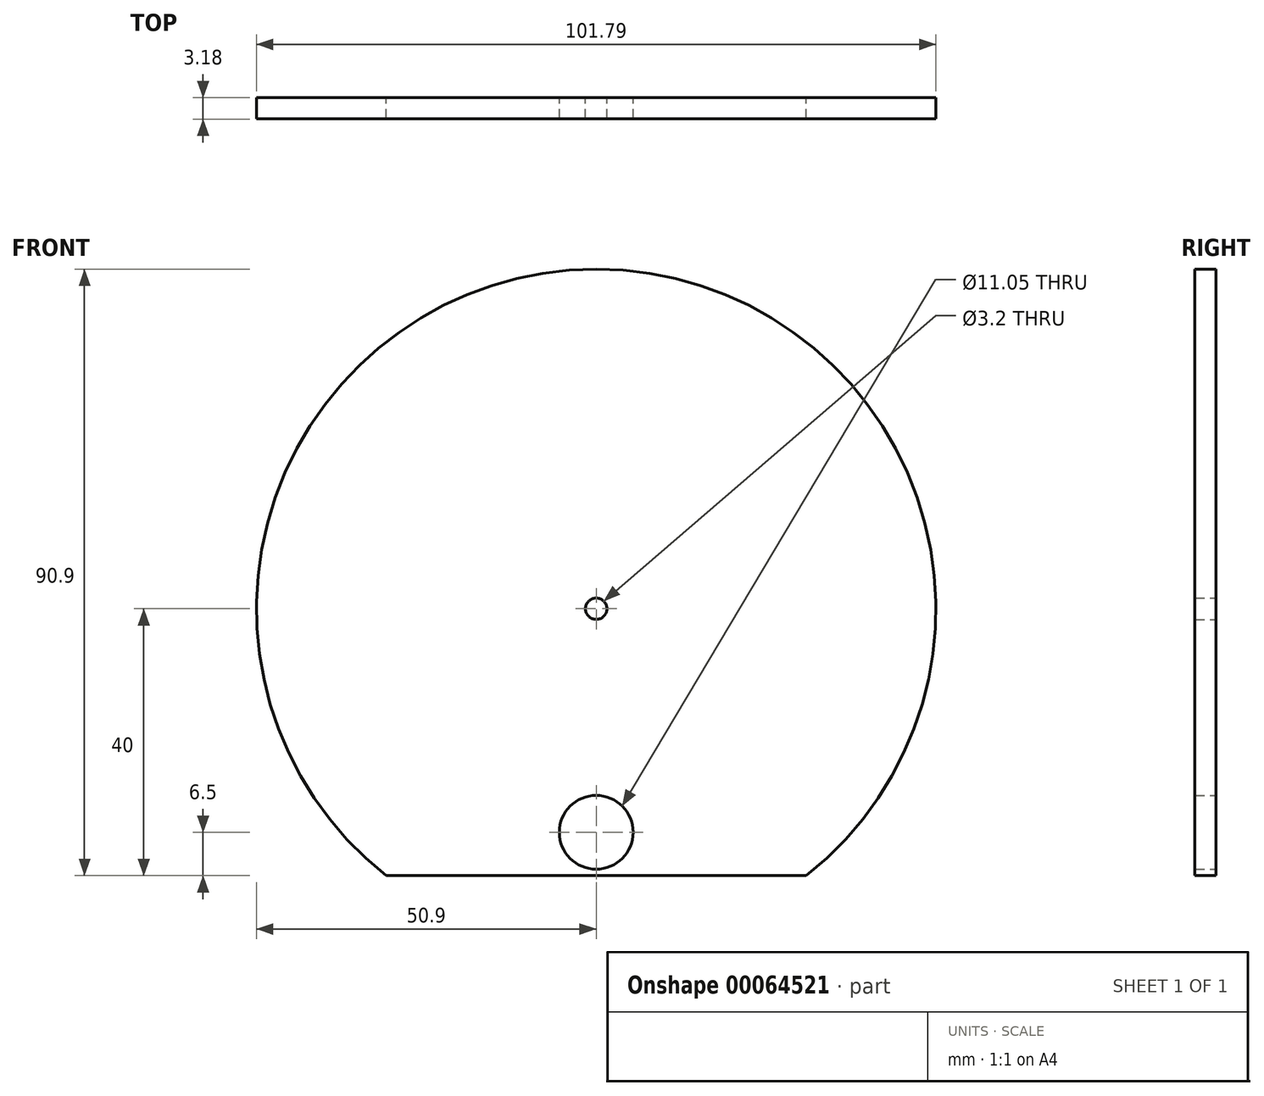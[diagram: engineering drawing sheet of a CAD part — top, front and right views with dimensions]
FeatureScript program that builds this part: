
annotation { "Feature Type Name" : "Feature", "Feature Type Description" : "" }
export const myFeature = defineFeature(function(context is Context, id is Id, definition is map)
    precondition{}
    {
        {
            var Q0;
            Q0=qCreatedBy(makeId("Front.planeOp"),FACE);
            var sketch = newSketch(context, id + "F0", { "sketchPlane" : qUnion([Q0])});
            skCircle(sketch, "E0", {"center": v(0, 0) * mm, "radius": 40 * mm});
            skCircle(sketch, "E1", {"center": v(0, 0) * mm, "radius": 50.9 * mm});
            skLineSegment(sketch, "E2.bottom", {"start": v(-55, -40) * mm, "end": v(55, -40) * mm});
            skLineSegment(sketch, "E2.top", {"start": v(-55, -70) * mm, "end": v(55, -70) * mm});
            skLineSegment(sketch, "E2.left", {"start": v(-55, -40) * mm, "end": v(-55, -70) * mm});
            skLineSegment(sketch, "E2.right", {"start": v(55, -40) * mm, "end": v(55, -70) * mm});
            skCircle(sketch, "E3", {"center": v(0, 0) * mm, "radius": 1.6 * mm});
            skCircle(sketch, "E4", {"center": v(0, -33.5) * mm, "radius": 5.52 * mm});
            skLineSegment(sketch, "E5.bottom", {"start": v(50, -45) * mm, "end": v(-50, -45) * mm});
            skLineSegment(sketch, "E5.top", {"start": v(50, -65) * mm, "end": v(-50, -65) * mm});
            skLineSegment(sketch, "E5.left", {"start": v(50, -45) * mm, "end": v(50, -65) * mm});
            skLineSegment(sketch, "E5.right", {"start": v(-50, -45) * mm, "end": v(-50, -65) * mm});
            skLineSegment(sketch, "E6", {"start": v(-50, -45) * mm, "end": v(-50, -40) * mm});
            skLineSegment(sketch, "E7", {"start": v(-50, -45) * mm, "end": v(-55, -45) * mm});
            skLineSegment(sketch, "E8", {"start": v(50, -65) * mm, "end": v(55, -65) * mm});
            skLineSegment(sketch, "E9", {"start": v(55, -65) * mm, "end": v(50, -65) * mm});
            skLineSegment(sketch, "E10", {"start": v(50, -70) * mm, "end": v(50, -65) * mm});
            skPoint(sketch, "E11", {"position": v(0, -65) * mm});
            skPoint(sketch, "E12", {"position": v(0, -45) * mm});
            skPoint(sketch, "E13", {"position": v(0, -40) * mm});
            skSolve(sketch);
        }
        {
            var Q0;
            Q0=makeQuery(id+"F0.imprint","IMPRINT",FACE,{"disambiguationData":[TD([[makeQuery(id+"F0.imprint","IMPRINT",EDGE,{"derivedFrom":sQuery(id+"F0.wireOp",EDGE,"E0")}),1.0]])]});
            var Q1;
            Q1=makeQuery(id+"F0.imprint","IMPRINT",FACE,{"disambiguationData":[TD([[makeQuery(id+"F0.imprint","IMPRINT",EDGE,{"derivedFrom":sQuery(id+"F0.wireOp",EDGE,"E0")}),-1.0]])]});
            extrude(context, id + "F1", {"entities" : qUnion([Q0, Q1]), "depth" : 3.17 * mm});
        }
    });
